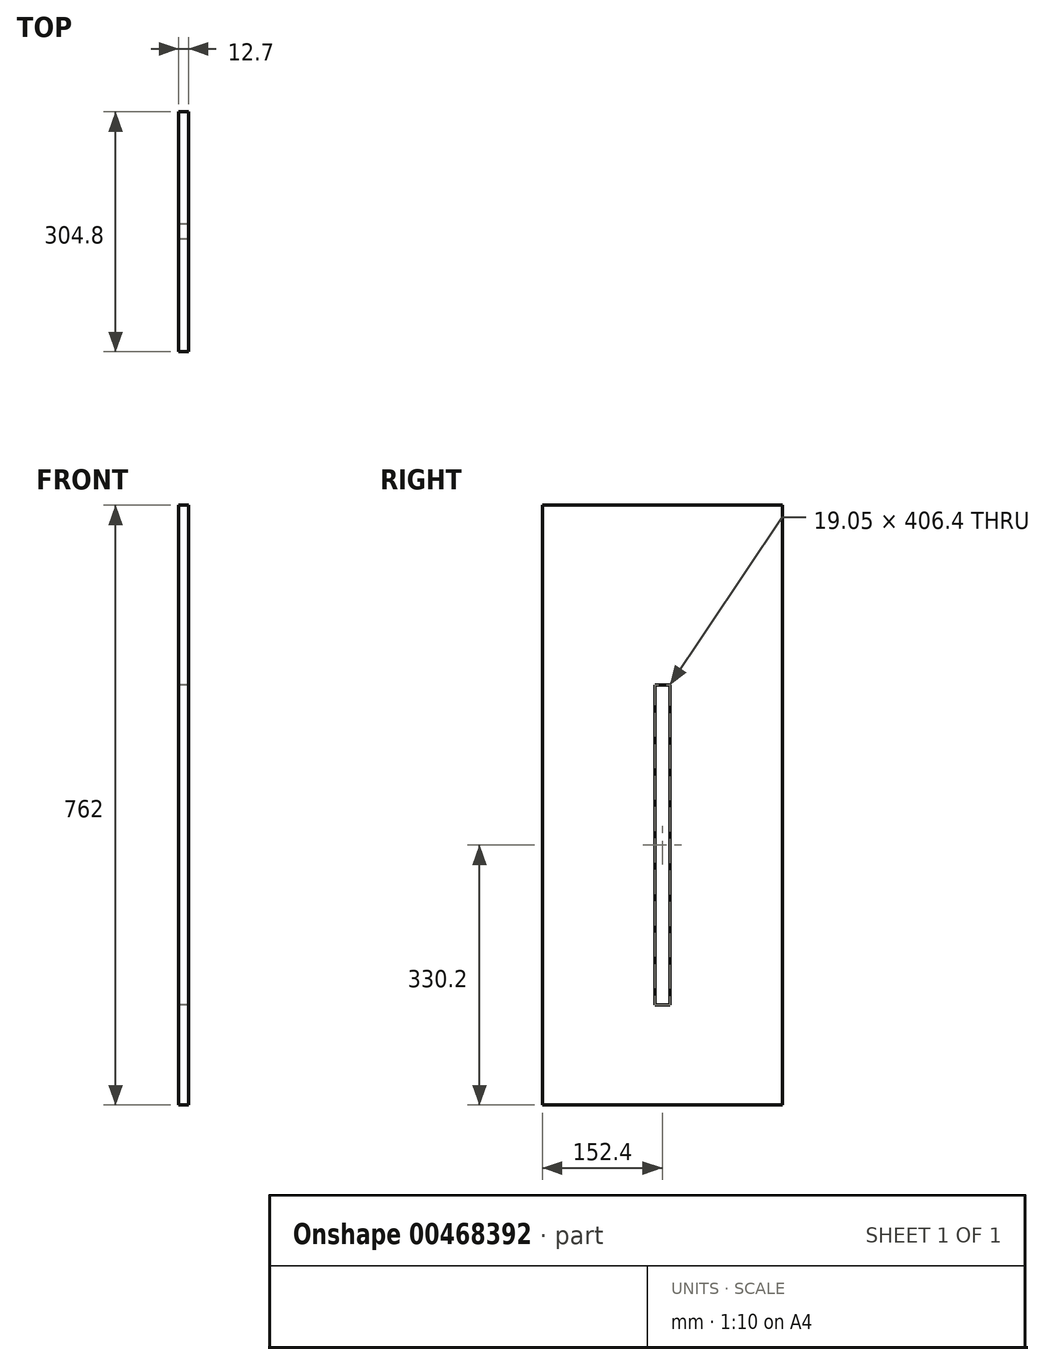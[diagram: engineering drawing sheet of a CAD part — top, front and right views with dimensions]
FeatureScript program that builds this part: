
annotation { "Feature Type Name" : "Feature", "Feature Type Description" : "" }
export const myFeature = defineFeature(function(context is Context, id is Id, definition is map)
    precondition{}
    {
        {
            var Q0;
            Q0=qCreatedBy(makeId("Right.planeOp"),FACE);
            var sketch = newSketch(context, id + "F0", { "sketchPlane" : qUnion([Q0])});
            skLineSegment(sketch, "E0", {"start": v(0, 0) * mm, "end": v(0, 762) * mm});
            skLineSegment(sketch, "E1", {"start": v(0, 762) * mm, "end": v(304.8, 762) * mm});
            skLineSegment(sketch, "E2", {"start": v(304.8, 762) * mm, "end": v(304.8, 0) * mm});
            skLineSegment(sketch, "E3", {"start": v(0, 0) * mm, "end": v(304.8, 0) * mm});
            skLineSegment(sketch, "E4.bottom", {"start": v(161.93, 127) * mm, "end": v(142.88, 127) * mm});
            skLineSegment(sketch, "E4.top", {"start": v(161.93, 533.4) * mm, "end": v(142.88, 533.4) * mm});
            skLineSegment(sketch, "E4.left", {"start": v(161.93, 127) * mm, "end": v(161.93, 533.4) * mm});
            skLineSegment(sketch, "E4.right", {"start": v(142.88, 127) * mm, "end": v(142.88, 533.4) * mm});
            skPoint(sketch, "E4.middle", {"position": v(152.4, 330.2) * mm});
            skSolve(sketch);
        }
        {
            var Q0;
            Q0 = qSketchRegion(id + "F0", true);
            extrude(context, id + "F1", {"entities" : qUnion([Q0]), "endBound" : BoundingType.SYMMETRIC, "depth" : 12.7 * mm});
        }
    });
